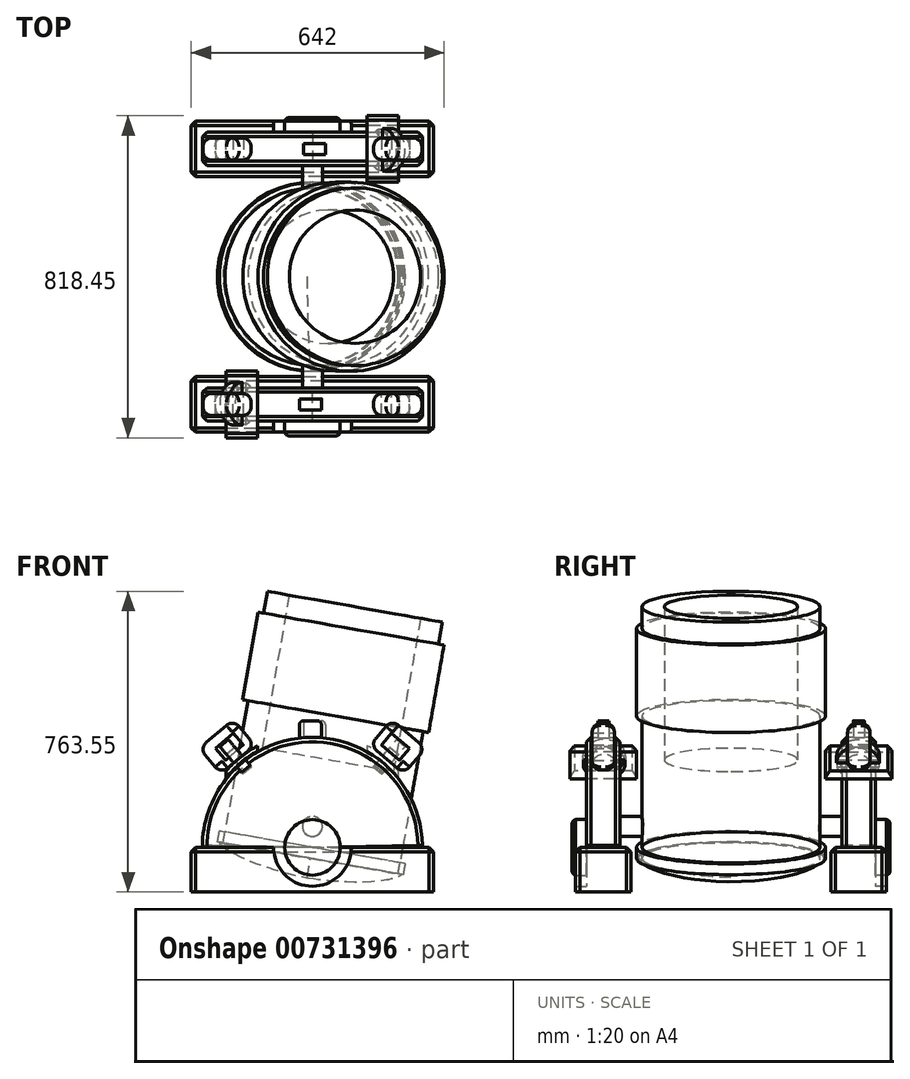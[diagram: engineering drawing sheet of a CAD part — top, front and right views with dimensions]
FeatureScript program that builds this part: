
annotation { "Feature Type Name" : "Feature", "Feature Type Description" : "" }
export const myFeature = defineFeature(function(context is Context, id is Id, definition is map)
    precondition{}
    {
        {
            var Q0;
            Q0=qCreatedBy(makeId("Top.planeOp"),FACE);
            var sketch = newSketch(context, id + "F0", { "sketchPlane" : qUnion([Q0])});
            skCircle(sketch, "E0", {"center": v(0, 0) * mm, "radius": 38.1 * mm});
            skCircle(sketch, "E1", {"center": v(0, 0) * mm, "radius": 50.8 * mm});
            skSolve(sketch);
        }
        {
            var Q0;
            Q0=makeQuery(id+"F0.imprint","IMPRINT",FACE,{"disambiguationData":[TD([[makeQuery(id+"F0.imprint","IMPRINT",EDGE,{"derivedFrom":sQuery(id+"F0.wireOp",EDGE,"E0")}),-1.0]])]});
            extrude(context, id + "F1", {"entities" : qUnion([Q0]), "depth" : 139.7 * mm, "offsetDistance" : 25.4 * mm});
        }
        {
            var Q0;
            Q0=makeQuery(id+"F0.imprint","IMPRINT",FACE,{"disambiguationData":[TD([[makeQuery(id+"F0.imprint","IMPRINT",EDGE,{"derivedFrom":sQuery(id+"F0.wireOp",EDGE,"E0")}),-1.0]])]});
            var Q1;
            Q1=makeQuery(id+"F0.imprint","IMPRINT",FACE,{"disambiguationData":[TD([[makeQuery(id+"F0.imprint","IMPRINT",EDGE,{"derivedFrom":sQuery(id+"F0.wireOp",EDGE,"E0")}),1.0]])]});
            extrude(context, id + "F2", {"entities" : qUnion([Q0, Q1]), "operationType" : NewBodyOperationType.ADD, "depth" : 50.8 * mm, "offsetDistance" : 25.4 * mm});
        }
        {
            var Q0;
            Q0=qCreatedBy(makeId("Top.planeOp"),FACE);
            cPlane(context, id + "F3", {"entities" : qUnion([Q0]), "cplaneType" : CPlaneType.OFFSET, "offset" : 76.2 * mm, "width" : 152.4 * mm, "height" : 152.4 * mm});
        }
        {
            var Q0;
            Q0=qCreatedBy(id+"F3.planeOp",FACE);
            var sketch = newSketch(context, id + "F4", { "sketchPlane" : qUnion([Q0])});
            skCircle(sketch, "E2", {"center": v(0, 0) * mm, "radius": 50.8 * mm});
            skCircle(sketch, "E3", {"center": v(0, 0) * mm, "radius": 53.98 * mm});
            skSolve(sketch);
        }
        {
            var Q0;
            Q0=makeQuery(id+"F4.imprint","IMPRINT",FACE,{"disambiguationData":[TD([[makeQuery(id+"F4.imprint","IMPRINT",EDGE,{"derivedFrom":sQuery(id+"F4.wireOp",EDGE,"E2")}),-1.0]])]});
            extrude(context, id + "F5", {"entities" : qUnion([Q0]), "operationType" : NewBodyOperationType.ADD, "depth" : 50.8 * mm, "offsetDistance" : 25.4 * mm});
        }
        {
            var Q0;
            Q0=qCreatedBy(makeId("Front.planeOp"),FACE);
            cPlane(context, id + "F6", {"entities" : qUnion([Q0]), "cplaneType" : CPlaneType.OFFSET, "offset" : 63.5 * mm, "width" : 152.4 * mm, "height" : 152.4 * mm});
        }
        {
            var Q0;
            Q0=qCreatedBy(id+"F6.planeOp",FACE);
            var sketch = newSketch(context, id + "F7", { "sketchPlane" : qUnion([Q0])});
            skArc(sketch, "E4", {"start": v(45.28, -43.66) * mm, "mid": v(43.66, 45.28) * mm, "end": v(-45.28, 43.66) * mm});
            skLineSegment(sketch, "E5", {"start": v(-45.28, 43.66) * mm, "end": v(45.28, -43.66) * mm});
            skSolve(sketch);
        }
        {
            var Q0;
            Q0=qSketchRegion(id+"F7",true);
            extrude(context, id + "F8", {"entities" : qUnion([Q0]), "depth" : 19.05 * mm});
        }
        {
            var Q0;
            Q0=qCreatedBy(makeId("Top.planeOp"),FACE);
            var sketch = newSketch(context, id + "F9", { "sketchPlane" : qUnion([Q0])});
            skLineSegment(sketch, "E6", {"start": v(0, 0) * mm, "end": v(0, -70.78) * mm});
            skSolve(sketch);
        }
        {
            var Q0;
            Q0=makeQuery(id+"F8.opExtrude","SWEPT_BODY",BODY,{"disambiguationData":[OSD([sQuery(id+"F7.wireOp",EDGE,"E4"),sQuery(id+"F7.wireOp",EDGE,"E5")])]});
            var Q1;
            Q1=sQuery(id+"F9.wireOp",EDGE,"E6");
            transform(context, id + "F10", {"entities" : qUnion([Q0]), "transformType" : TransformType.ROTATION, "transformAxis" : qUnion([Q1]), "angle" : 45 * degree, "makeCopy" : false});
        }
        {
            var Q0;
            Q0=qCreatedBy(makeId("Top.planeOp"),FACE);
            var sketch = newSketch(context, id + "F11", { "sketchPlane" : qUnion([Q0])});
            skLineSegment(sketch, "E7.0.0", {"start": v(-62.9, -63.5) * mm, "end": v(62.9, -63.5) * mm});
            skLineSegment(sketch, "E7.0.1", {"start": v(62.9, -63.5) * mm, "end": v(62.9, -82.55) * mm});
            skLineSegment(sketch, "E7.0.2", {"start": v(62.9, -82.55) * mm, "end": v(-62.9, -82.55) * mm});
            skLineSegment(sketch, "E7.0.3", {"start": v(-62.9, -82.55) * mm, "end": v(-62.9, -63.5) * mm});
            skLineSegment(sketch, "E8", {"start": v(-62.9, -82.55) * mm, "end": v(-69.24, -82.55) * mm});
            skLineSegment(sketch, "E9", {"start": v(-62.9, -82.55) * mm, "end": v(-62.9, -88.9) * mm});
            skLineSegment(sketch, "E10.MirrorCS", {"start": v(62.9, -82.55) * mm, "end": v(62.9, -88.9) * mm});
            skLineSegment(sketch, "E11.MirrorCS", {"start": v(62.9, -82.55) * mm, "end": v(69.24, -82.55) * mm});
            skLineSegment(sketch, "E12", {"start": v(62.9, -63.5) * mm, "end": v(62.9, -57.15) * mm});
            skLineSegment(sketch, "E13", {"start": v(62.9, -63.5) * mm, "end": v(69.24, -63.5) * mm});
            skLineSegment(sketch, "E14.bottom", {"start": v(-69.24, -88.9) * mm, "end": v(69.24, -88.9) * mm});
            skLineSegment(sketch, "E14.top", {"start": v(-69.24, -57.15) * mm, "end": v(69.24, -57.15) * mm});
            skLineSegment(sketch, "E14.left", {"start": v(-69.24, -88.9) * mm, "end": v(-69.24, -57.15) * mm});
            skLineSegment(sketch, "E14.right", {"start": v(69.24, -88.9) * mm, "end": v(69.24, -57.15) * mm});
            skSolve(sketch);
        }
        {
            var Q0;
            {var subQ0=sQuery(id+"F11.wireOp",EDGE,"E12");Q0=makeQuery(id+"F11.imprint","IMPRINT",FACE,{"disambiguationData":[TD([[makeQuery(id+"F11.imprint","IMPRINT",EDGE,{"derivedFrom":subQ0}),-1.0]])]});}
            var Q1;
            Q1=makeQuery(id+"F11.imprint","IMPRINT",FACE,{"disambiguationData":[TD([[makeQuery(id+"F11.imprint","IMPRINT",EDGE,{"derivedFrom":sQuery(id+"F11.wireOp",EDGE,"E7.0.1")}),1.0]])]});
            var Q2;
            Q2=makeQuery(id+"F11.imprint","IMPRINT",FACE,{"disambiguationData":[TD([[makeQuery(id+"F11.imprint","IMPRINT",EDGE,{"derivedFrom":sQuery(id+"F11.wireOp",EDGE,"E7.0.0")}),-1.0]])]});
            var Q3;
            Q3=makeQuery(id+"F11.imprint","IMPRINT",FACE,{"disambiguationData":[TD([[makeQuery(id+"F11.imprint","IMPRINT",EDGE,{"derivedFrom":sQuery(id+"F11.wireOp",EDGE,"E7.0.0")}),1.0]])]});
            var Q4;
            {var subQ0=sQuery(id+"F11.wireOp",EDGE,"E11.MirrorCS");Q4=makeQuery(id+"F11.imprint","IMPRINT",FACE,{"disambiguationData":[TD([[makeQuery(id+"F11.imprint","IMPRINT",EDGE,{"derivedFrom":subQ0}),-1.0]])]});}
            var Q5;
            Q5=makeQuery(id+"F11.imprint","IMPRINT",FACE,{"disambiguationData":[TD([[makeQuery(id+"F11.imprint","IMPRINT",EDGE,{"derivedFrom":sQuery(id+"F11.wireOp",EDGE,"E7.0.2")}),1.0]])]});
            var Q6;
            {var subQ0=sQuery(id+"F11.wireOp",EDGE,"E8");Q6=makeQuery(id+"F11.imprint","IMPRINT",FACE,{"disambiguationData":[TD([[makeQuery(id+"F11.imprint","IMPRINT",EDGE,{"derivedFrom":subQ0}),1.0]])]});}
            extrude(context, id + "F12", {"entities" : qUnion([Q0, Q1, Q2, Q3, Q4, Q5, Q6]), "oppositeDirection" : true, "depth" : 25.4 * mm});
        }
        {
            var Q0;
            Q0=makeQuery(id+"F8.opExtrude","CAP_FACE",FACE,{"disambiguationData":[OSD([sQuery(id+"F7.wireOp",EDGE,"E4"),sQuery(id+"F7.wireOp",EDGE,"E5")])],"isStart":false});
            var sketch = newSketch(context, id + "F13", { "sketchPlane" : qUnion([Q0])});
            skCircle(sketch, "E15", {"center": v(0, 0) * mm, "radius": 22.23 * mm});
            skCircle(sketch, "E16", {"center": v(0, 0) * mm, "radius": 15.88 * mm});
            skSolve(sketch);
        }
        {
            var Q0;
            {var subQ0=sQuery(id+"F13.wireOp",EDGE,"E16");var subQ1=makeQuery(id+"F8.opExtrude","CAP_EDGE",EDGE,{"disambiguationData":[OSD([sQuery(id+"F7.wireOp",EDGE,"E5")])],"isStart":false});var subQ2=makeQuery(id+"F13.imprint","INTERSECT",VERTEX,{"disambiguationData":[OD(0.0)],"derivedFrom":[subQ1,subQ0]});Q0=makeQuery(id+"F13.imprint","IMPRINT",FACE,{"disambiguationData":[TD([[makeQuery(id+"F13.imprint","IMPRINT",EDGE,{"disambiguationData":[TD([[subQ2,-1.0]])],"derivedFrom":subQ0}),1.0]])]});}
            var Q1;
            {var subQ0=sQuery(id+"F13.wireOp",EDGE,"E16");var subQ1=makeQuery(id+"F8.opExtrude","CAP_EDGE",EDGE,{"disambiguationData":[OSD([sQuery(id+"F7.wireOp",EDGE,"E5")])],"isStart":false});var subQ2=makeQuery(id+"F13.imprint","INTERSECT",VERTEX,{"disambiguationData":[OD(0.0)],"derivedFrom":[subQ1,subQ0]});Q1=makeQuery(id+"F13.imprint","IMPRINT",FACE,{"disambiguationData":[TD([[makeQuery(id+"F13.imprint","IMPRINT",EDGE,{"disambiguationData":[TD([[subQ2,1.0]])],"derivedFrom":subQ0}),1.0]])]});}
            extrude(context, id + "F14", {"entities" : qUnion([Q0, Q1]), "operationType" : NewBodyOperationType.ADD, "depth" : 8.38 * mm, "offsetDistance" : 25.4 * mm});
        }
        {
            var Q0;
            {var subQ0=sQuery(id+"F13.wireOp",EDGE,"E15");var subQ1=makeQuery(id+"F8.opExtrude","CAP_EDGE",EDGE,{"disambiguationData":[OSD([sQuery(id+"F7.wireOp",EDGE,"E5")])],"isStart":false});var subQ2=makeQuery(id+"F13.imprint","INTERSECT",VERTEX,{"disambiguationData":[OD(0.0)],"derivedFrom":[subQ1,subQ0]});Q0=makeQuery(id+"F13.imprint","IMPRINT",FACE,{"disambiguationData":[TD([[makeQuery(id+"F13.imprint","IMPRINT",EDGE,{"disambiguationData":[TD([[subQ2,-1.0]])],"derivedFrom":subQ0}),1.0]])]});}
            var Q1;
            {var subQ0=sQuery(id+"F13.wireOp",EDGE,"E15");var subQ1=makeQuery(id+"F8.opExtrude","CAP_EDGE",EDGE,{"disambiguationData":[OSD([sQuery(id+"F7.wireOp",EDGE,"E5")])],"isStart":false});var subQ2=makeQuery(id+"F13.imprint","INTERSECT",VERTEX,{"disambiguationData":[OD(0.0)],"derivedFrom":[subQ1,subQ0]});Q1=makeQuery(id+"F13.imprint","IMPRINT",FACE,{"disambiguationData":[TD([[makeQuery(id+"F13.imprint","IMPRINT",EDGE,{"disambiguationData":[TD([[subQ2,1.0]])],"derivedFrom":subQ0}),1.0]])]});}
            extrude(context, id + "F15", {"entities" : qUnion([Q0, Q1]), "operationType" : NewBodyOperationType.ADD, "depth" : 6.35 * mm, "offsetDistance" : 25.4 * mm});
        }
        {
            var Q0;
            Q0=makeQuery(id+"F15.opExtrude","CAP_EDGE",EDGE,{"disambiguationData":[OSD([sQuery(id+"F13.wireOp",EDGE,"E15")])],"isStart":false});
            var Q1;
            Q1=makeQuery(id+"F14.opExtrude","CAP_EDGE",EDGE,{"disambiguationData":[OSD([sQuery(id+"F13.wireOp",EDGE,"E16")])],"isStart":false});
            fillet(context, id + "F16", {"entities" : qUnion([Q0, Q1]), "radius" : 2.54 * mm, "tangentPropagation" : true, "allowEdgeOverflow" : false});
        }
        {
            var Q0;
            Q0=qSketchRegion(id+"F13",true);
            var Q1;
            Q1=sQuery(id+"F13.wireOp",EDGE,"E15");
            extrude(context, id + "F17", {"entities" : qUnion([Q0]), "operationType" : NewBodyOperationType.REMOVE, "surfaceEntities" : qUnion([Q1]), "depth" : 25.4 * mm});
        }
        {
            var Q0;
            Q0=makeQuery(id+"F8.opExtrude","SWEPT_BODY",BODY,{"disambiguationData":[OSD([sQuery(id+"F7.wireOp",EDGE,"E4"),sQuery(id+"F7.wireOp",EDGE,"E5")])]});
            var Q1;
            Q1=makeQuery(id+"F14.opExtrude","SWEPT_BODY",BODY,{"disambiguationData":[OSD([sQuery(id+"F13.wireOp",EDGE,"E16")])]});
            var Q2;
            Q2=makeQuery(id+"F15.opExtrude","SWEPT_BODY",BODY,{"disambiguationData":[OSD([sQuery(id+"F13.wireOp",EDGE,"E15"),sQuery(id+"F13.wireOp",EDGE,"E16")])]});
            var Q3;
            Q3=makeQuery(id+"F17.boolean.opBoolean","SPLIT",BODY,{"disambiguationData":[OD(0.0)],"derivedFrom":makeQuery(id+"F12.opExtrude","SWEPT_BODY",BODY,{"disambiguationData":[OSD([sQuery(id+"F11.wireOp",EDGE,"E7.0.0"),sQuery(id+"F11.wireOp",EDGE,"E7.0.1"),sQuery(id+"F11.wireOp",EDGE,"E7.0.2"),sQuery(id+"F11.wireOp",EDGE,"E7.0.3"),sQuery(id+"F11.wireOp",EDGE,"E14.bottom"),sQuery(id+"F11.wireOp",EDGE,"E14.top"),sQuery(id+"F11.wireOp",EDGE,"E14.left"),sQuery(id+"F11.wireOp",EDGE,"E14.right")])]})});
            var Q4;
            Q4=makeQuery(id+"F17.boolean.opBoolean","SPLIT",BODY,{"disambiguationData":[OD(1.0)],"derivedFrom":makeQuery(id+"F12.opExtrude","SWEPT_BODY",BODY,{"disambiguationData":[OSD([sQuery(id+"F11.wireOp",EDGE,"E7.0.0"),sQuery(id+"F11.wireOp",EDGE,"E7.0.1"),sQuery(id+"F11.wireOp",EDGE,"E7.0.2"),sQuery(id+"F11.wireOp",EDGE,"E7.0.3"),sQuery(id+"F11.wireOp",EDGE,"E14.bottom"),sQuery(id+"F11.wireOp",EDGE,"E14.top"),sQuery(id+"F11.wireOp",EDGE,"E14.left"),sQuery(id+"F11.wireOp",EDGE,"E14.right")])]})});
            var Q5;
            Q5=makeQuery(id+"F1.opExtrude","SWEPT_FACE",FACE,{"disambiguationData":[OSD([sQuery(id+"F0.wireOp",EDGE,"E0")])]});
            transform(context, id + "F18", {"entities" : qUnion([Q0, Q1, Q2, Q3, Q4]), "transformType" : TransformType.ROTATION, "transformAxis" : qUnion([Q5]), "angle" : 180 * degree, "makeCopy" : true});
        }
        {
            var Q0;
            Q0=makeQuery(id+"F18.opPattern","COPY",BODY,{"derivedFrom":makeQuery(id+"F8.opExtrude","SWEPT_BODY",BODY,{"disambiguationData":[OSD([sQuery(id+"F7.wireOp",EDGE,"E4"),sQuery(id+"F7.wireOp",EDGE,"E5")])]}),"instanceName":"1"});
            var Q1;
            Q1=makeQuery(id+"F18.opPattern","COPY",BODY,{"derivedFrom":makeQuery(id+"F14.opExtrude","SWEPT_BODY",BODY,{"disambiguationData":[OSD([sQuery(id+"F13.wireOp",EDGE,"E16")])]}),"instanceName":"1"});
            var Q2;
            Q2=makeQuery(id+"F18.opPattern","COPY",BODY,{"derivedFrom":makeQuery(id+"F15.opExtrude","SWEPT_BODY",BODY,{"disambiguationData":[OSD([sQuery(id+"F13.wireOp",EDGE,"E15"),sQuery(id+"F13.wireOp",EDGE,"E16")])]}),"instanceName":"1"});
            var Q3;
            Q3=makeQuery(id+"F18.opPattern","COPY",BODY,{"derivedFrom":makeQuery(id+"F17.boolean.opBoolean","SPLIT",BODY,{"disambiguationData":[OD(0.0)],"derivedFrom":makeQuery(id+"F12.opExtrude","SWEPT_BODY",BODY,{"disambiguationData":[OSD([sQuery(id+"F11.wireOp",EDGE,"E7.0.0"),sQuery(id+"F11.wireOp",EDGE,"E7.0.1"),sQuery(id+"F11.wireOp",EDGE,"E7.0.2"),sQuery(id+"F11.wireOp",EDGE,"E7.0.3"),sQuery(id+"F11.wireOp",EDGE,"E14.bottom"),sQuery(id+"F11.wireOp",EDGE,"E14.top"),sQuery(id+"F11.wireOp",EDGE,"E14.left"),sQuery(id+"F11.wireOp",EDGE,"E14.right")])]})}),"instanceName":"1"});
            var Q4;
            Q4=makeQuery(id+"F18.opPattern","COPY",BODY,{"derivedFrom":makeQuery(id+"F17.boolean.opBoolean","SPLIT",BODY,{"disambiguationData":[OD(1.0)],"derivedFrom":makeQuery(id+"F12.opExtrude","SWEPT_BODY",BODY,{"disambiguationData":[OSD([sQuery(id+"F11.wireOp",EDGE,"E7.0.0"),sQuery(id+"F11.wireOp",EDGE,"E7.0.1"),sQuery(id+"F11.wireOp",EDGE,"E7.0.2"),sQuery(id+"F11.wireOp",EDGE,"E7.0.3"),sQuery(id+"F11.wireOp",EDGE,"E14.bottom"),sQuery(id+"F11.wireOp",EDGE,"E14.top"),sQuery(id+"F11.wireOp",EDGE,"E14.left"),sQuery(id+"F11.wireOp",EDGE,"E14.right")])]})}),"instanceName":"1"});
            deleteBodies(context, id + "F19", {"entities" : qUnion([Q0, Q1, Q2, Q3, Q4])});
        }
        {
            var Q0;
            {var subQ1=sQuery(id+"F11.wireOp",EDGE,"E14.left");var subQ3=sQuery(id+"F11.wireOp",EDGE,"E14.bottom");Q0=makeQuery(id+"F17.boolean.opBoolean","SPLIT",FACE,{"disambiguationData":[TD([makeQuery(id+"F12.opExtrude","SWEPT_FACE",FACE,{"disambiguationData":[OSD([subQ1])]})])],"derivedFrom":makeQuery(id+"F12.opExtrude","SWEPT_FACE",FACE,{"disambiguationData":[OSD([subQ3])]})});}
            cPlane(context, id + "F20", {"entities" : qUnion([Q0]), "cplaneType" : CPlaneType.OFFSET, "offset" : 3.17 * mm, "width" : 152.4 * mm, "height" : 152.4 * mm});
        }
        {
            var Q0;
            Q0=qCreatedBy(id+"F20.planeOp",FACE);
            var sketch = newSketch(context, id + "F21", { "sketchPlane" : qUnion([Q0])});
            skArc(sketch, "E17.0", {"start": v(62.9, 1.15) * mm, "mid": v(-1.15, 62.9) * mm, "end": v(-62.9, -1.15) * mm});
            skLineSegment(sketch, "E18.0", {"start": v(-69.24, -25.4) * mm, "end": v(69.24, -25.4) * mm});
            skLineSegment(sketch, "E19", {"start": v(-49.3, -25.4) * mm, "end": v(-49.3, 43.8) * mm});
            skLineSegment(sketch, "E20", {"start": v(-49.3, -25.4) * mm, "end": v(-31.25, -25.4) * mm});
            skLineSegment(sketch, "E21", {"start": v(-31.25, -25.4) * mm, "end": v(-31.25, 58.08) * mm});
            skArc(sketch, "E22", {"start": v(-31.25, 58.08) * mm, "mid": v(-40.9, 51.74) * mm, "end": v(-49.3, 43.8) * mm});
            skArc(sketch, "E23.trimOffspring", {"start": v(-60.86, -25.4) * mm, "mid": v(0, -65.95) * mm, "end": v(60.86, -25.4) * mm});
            skSolve(sketch);
        }
        {
            var Q0;
            {var subQ5=sQuery(id+"F21.wireOp",EDGE,"E20");Q0=makeQuery(id+"F21.imprint","IMPRINT",FACE,{"disambiguationData":[TD([[makeQuery(id+"F21.imprint","IMPRINT",EDGE,{"derivedFrom":subQ5}),1.0]])]});}
            var Q1;
            {var subQ5=sQuery(id+"F21.wireOp",EDGE,"E22");Q1=makeQuery(id+"F21.imprint","IMPRINT",FACE,{"disambiguationData":[TD([[makeQuery(id+"F21.imprint","IMPRINT",EDGE,{"derivedFrom":subQ5}),1.0]])]});}
            extrude(context, id + "F22", {"entities" : qUnion([Q0, Q1]), "oppositeDirection" : true, "depth" : 38.1 * mm});
        }
        {
            var Q0;
            Q0=makeQuery(id+"F8.opExtrude","CAP_FACE",FACE,{"disambiguationData":[OSD([sQuery(id+"F7.wireOp",EDGE,"E4"),sQuery(id+"F7.wireOp",EDGE,"E5")])],"isStart":false});
            cPlane(context, id + "F23", {"entities" : qUnion([Q0]), "cplaneType" : CPlaneType.OFFSET, "offset" : 9.52 * mm, "oppositeDirection" : true, "width" : 152.4 * mm, "height" : 152.4 * mm});
        }
        {
            var Q0;
            Q0=qCreatedBy(id+"F23.planeOp",FACE);
            var sketch = newSketch(context, id + "F24", { "sketchPlane" : qUnion([Q0])});
            skPoint(sketch, "E24.0", {"position": v(-1.15, 62.9) * mm});
            skLineSegment(sketch, "E25.bottom", {"start": v(5.2, 72.42) * mm, "end": v(-7.5, 72.42) * mm});
            skLineSegment(sketch, "E25.top", {"start": v(5.2, 53.37) * mm, "end": v(-7.5, 53.37) * mm});
            skLineSegment(sketch, "E25.left", {"start": v(5.2, 72.42) * mm, "end": v(5.2, 53.37) * mm});
            skLineSegment(sketch, "E25.right", {"start": v(-7.5, 72.42) * mm, "end": v(-7.5, 53.37) * mm});
            skSolve(sketch);
        }
        {
            var Q0;
            Q0=makeQuery(id+"F24.imprint","IMPRINT",FACE,{"disambiguationData":[TD([[makeQuery(id+"F24.imprint","IMPRINT",EDGE,{"derivedFrom":sQuery(id+"F24.wireOp",EDGE,"E25.bottom")}),1.0]])]});
            extrude(context, id + "F25", {"entities" : qUnion([Q0]), "operationType" : NewBodyOperationType.ADD, "endBound" : BoundingType.SYMMETRIC, "depth" : 6.35 * mm, "offsetDistance" : 25.4 * mm});
        }
        {
            var Q0;
            Q0=makeQuery(id+"F25.opExtrude","SWEPT_EDGE",EDGE,{"disambiguationData":[OSD([sQuery(id+"F24.wireOp",EDGE,"E25.bottom"),sQuery(id+"F24.wireOp",EDGE,"E25.right")])]});
            var Q1;
            Q1=makeQuery(id+"F25.opExtrude","SWEPT_EDGE",EDGE,{"disambiguationData":[OSD([sQuery(id+"F24.wireOp",EDGE,"E25.bottom"),sQuery(id+"F24.wireOp",EDGE,"E25.left")])]});
            fillet(context, id + "F26", {"entities" : qUnion([Q0, Q1]), "radius" : 2.54 * mm, "tangentPropagation" : true, "allowEdgeOverflow" : false});
        }
        {
            var Q0;
            Q0=makeQuery(id+"F22.opExtrude","CAP_EDGE",EDGE,{"disambiguationData":[OSD([sQuery(id+"F21.wireOp",EDGE,"E22")])],"isStart":true});
            var Q1;
            Q1=makeQuery(id+"FDD8fb37NUxeniG_7.opPattern","COPY",EDGE,{"derivedFrom":makeQuery(id+"F22.opExtrude","CAP_EDGE",EDGE,{"disambiguationData":[OSD([sQuery(id+"F21.wireOp",EDGE,"E22")])],"isStart":true}),"instanceName":"1"});
            var Q2;
            {var subQ0=sQuery(id+"F11.wireOp",EDGE,"E14.left");var subQ1=sQuery(id+"F11.wireOp",EDGE,"E14.bottom");Q2=makeQuery(id+"F17.boolean.opBoolean","SPLIT",EDGE,{"disambiguationData":[TD([makeQuery(id+"F12.opExtrude","SWEPT_FACE",FACE,{"disambiguationData":[OSD([subQ0])]})])],"derivedFrom":makeQuery(id+"F12.opExtrude","CAP_EDGE",EDGE,{"disambiguationData":[OSD([subQ1])],"isStart":true})});}
            var Q3;
            {var subQ0=sQuery(id+"F11.wireOp",EDGE,"E14.right");var subQ1=sQuery(id+"F11.wireOp",EDGE,"E14.bottom");Q3=makeQuery(id+"F17.boolean.opBoolean","SPLIT",EDGE,{"disambiguationData":[TD([makeQuery(id+"F12.opExtrude","SWEPT_FACE",FACE,{"disambiguationData":[OSD([subQ0])]})])],"derivedFrom":makeQuery(id+"F12.opExtrude","CAP_EDGE",EDGE,{"disambiguationData":[OSD([subQ1])],"isStart":true})});}
            var Q4;
            Q4=makeQuery(id+"F12.opExtrude","CAP_EDGE",EDGE,{"disambiguationData":[OSD([sQuery(id+"F11.wireOp",EDGE,"E14.left")])],"isStart":true});
            var Q5;
            Q5=makeQuery(id+"F12.opExtrude","SWEPT_EDGE",EDGE,{"disambiguationData":[OSD([sQuery(id+"F11.wireOp",EDGE,"E14.bottom"),sQuery(id+"F11.wireOp",EDGE,"E14.left")])]});
            var Q6;
            Q6=makeQuery(id+"F22.opExtrude","CAP_EDGE",EDGE,{"disambiguationData":[OSD([sQuery(id+"F21.wireOp",EDGE,"E22")])],"isStart":false});
            var Q7;
            Q7=makeQuery(id+"F8.opExtrude","CAP_EDGE",EDGE,{"disambiguationData":[OSD([sQuery(id+"F7.wireOp",EDGE,"E4")])],"isStart":false});
            var Q8;
            Q8=makeQuery(id+"F8.opExtrude","CAP_EDGE",EDGE,{"disambiguationData":[OSD([sQuery(id+"F7.wireOp",EDGE,"E4")])],"isStart":true});
            var Q9;
            Q9=makeQuery(id+"F12.opExtrude","CAP_EDGE",EDGE,{"disambiguationData":[OSD([sQuery(id+"F11.wireOp",EDGE,"E14.top")])],"isStart":true});
            var Q10;
            Q10=makeQuery(id+"F12.opExtrude","SWEPT_EDGE",EDGE,{"disambiguationData":[OSD([sQuery(id+"F11.wireOp",EDGE,"E14.top"),sQuery(id+"F11.wireOp",EDGE,"E14.left")])]});
            var Q11;
            Q11=makeQuery(id+"F12.opExtrude","SWEPT_EDGE",EDGE,{"disambiguationData":[OSD([sQuery(id+"F11.wireOp",EDGE,"E14.bottom"),sQuery(id+"F11.wireOp",EDGE,"E14.right")])]});
            var Q12;
            Q12=makeQuery(id+"F12.opExtrude","CAP_EDGE",EDGE,{"disambiguationData":[OSD([sQuery(id+"F11.wireOp",EDGE,"E14.right")])],"isStart":true});
            var Q13;
            Q13=makeQuery(id+"FDD8fb37NUxeniG_7.opPattern","COPY",EDGE,{"derivedFrom":makeQuery(id+"F22.opExtrude","CAP_EDGE",EDGE,{"disambiguationData":[OSD([sQuery(id+"F21.wireOp",EDGE,"E22")])],"isStart":false}),"instanceName":"1"});
            var Q14;
            Q14=makeQuery(id+"F12.opExtrude","SWEPT_EDGE",EDGE,{"disambiguationData":[OSD([sQuery(id+"F11.wireOp",EDGE,"E14.top"),sQuery(id+"F11.wireOp",EDGE,"E14.right")])]});
            chamfer(context, id + "F27", {"entities" : qUnion([Q0, Q1, Q2, Q3, Q4, Q5, Q6, Q7, Q8, Q9, Q10, Q11, Q12, Q13, Q14]), "width" : 2.54 * mm, "tangentPropagation" : true});
        }
        {
            var Q0;
            {var subQ0=sQuery(id+"F21.wireOp",EDGE,"E22");Q0=makeQuery(id+"F27.opChamfer","BLEND_EDGE",EDGE,{"blendedFrom":[makeQuery(id+"F22.opExtrude","CAP_EDGE",EDGE,{"disambiguationData":[OSD([subQ0])],"isStart":true}),makeQuery(id+"F22.opExtrude","CAP_FACE",FACE,{"disambiguationData":[OSD([sQuery(id+"F21.wireOp",EDGE,"E19"),sQuery(id+"F21.wireOp",EDGE,"E21"),subQ0,sQuery(id+"F21.wireOp",EDGE,"E20")])],"isStart":true})],"blendedInto":[makeQuery(id+"F22.opExtrude","CAP_FACE",FACE,{"disambiguationData":[OSD([sQuery(id+"F21.wireOp",EDGE,"E19"),sQuery(id+"F21.wireOp",EDGE,"E21"),subQ0,sQuery(id+"F21.wireOp",EDGE,"E20")])],"isStart":true})]});}
            cPoint(context, id + "F28", {"entities" : qUnion([Q0]), "parameter" : 0.5});
        }
        {
            var Q0;
            {var subQ0=sQuery(id+"F7.wireOp",EDGE,"E4");Q0=makeQuery(id+"F27.opChamfer","BLEND_EDGE",EDGE,{"blendedFrom":[makeQuery(id+"F8.opExtrude","CAP_EDGE",EDGE,{"disambiguationData":[OSD([subQ0])],"isStart":false}),makeQuery(id+"F8.opExtrude","SWEPT_FACE",FACE,{"disambiguationData":[OSD([subQ0])]})],"blendedInto":[makeQuery(id+"F8.opExtrude","SWEPT_FACE",FACE,{"disambiguationData":[OSD([subQ0])]})]});}
            var Q1;
            Q1=qCreatedBy(id+"F28",VERTEX);
            cPlane(context, id + "F29", {"entities" : qUnion([Q0, Q1]), "cplaneType" : CPlaneType.CURVE_POINT, "offset" : 25.4 * mm, "width" : 152.4 * mm, "height" : 152.4 * mm});
        }
        {
            var Q0;
            Q0=qCreatedBy(id+"F29.planeOp",FACE);
            var sketch = newSketch(context, id + "F30", { "sketchPlane" : qUnion([Q0])});
            skLineSegment(sketch, "E26", {"start": v(-76.83, 65.95) * mm, "end": v(-68.32, 65.95) * mm});
            skCircle(sketch, "E27", {"center": v(-72.58, 65.95) * mm, "radius": 12.21 * mm});
            skCircle(sketch, "E28", {"center": v(-72.58, 65.95) * mm, "radius": 6.35 * mm});
            skSolve(sketch);
        }
        {
            var Q0;
            {var subQ0=sQuery(id+"F30.wireOp",EDGE,"E27");var subQ1=sQuery(id+"F30.wireOp",EDGE,"E26");var subQ2=makeQuery(id+"F30.imprint","INTERSECT",VERTEX,{"disambiguationData":[OD(0.0)],"derivedFrom":[subQ1,subQ0]});Q0=makeQuery(id+"F30.imprint","IMPRINT",FACE,{"disambiguationData":[TD([[makeQuery(id+"F30.imprint","IMPRINT",EDGE,{"disambiguationData":[TD([[subQ2,-1.0]])],"derivedFrom":subQ1}),1.0]])]});}
            var Q1;
            Q1=makeQuery(id+"F30.imprint","IMPRINT",FACE,{"disambiguationData":[TD([[makeQuery(id+"F30.imprint","IMPRINT",EDGE,{"derivedFrom":sQuery(id+"F30.wireOp",EDGE,"E27")}),1.0]])]});
            extrude(context, id + "F31", {"entities" : qUnion([Q0, Q1]), "operationType" : NewBodyOperationType.ADD, "endBound" : BoundingType.SYMMETRIC, "depth" : 6.35 * mm, "offsetDistance" : 25.4 * mm});
        }
        {
            var Q0;
            Q0=qCreatedBy(id+"F29.planeOp",FACE);
            var sketch = newSketch(context, id + "F32", { "sketchPlane" : qUnion([Q0])});
            skLineSegment(sketch, "E29.0", {"start": v(-66.23, 65.95) * mm, "end": v(-66.23, 65.95) * mm});
            skCircle(sketch, "E30", {"center": v(-72.58, 65.95) * mm, "radius": 6.35 * mm});
            skSolve(sketch);
        }
        {
            var Q0;
            Q0=qCreatedBy(id+"F23.planeOp",FACE);
            var sketch = newSketch(context, id + "F33", { "sketchPlane" : qUnion([Q0])});
            skLineSegment(sketch, "E31.0", {"start": v(-46.74, 55.16) * mm, "end": v(-38.53, 45.47) * mm});
            skLineSegment(sketch, "E32", {"start": v(-42.63, 50.32) * mm, "end": v(-52.32, 42.1) * mm});
            skLineSegment(sketch, "E33", {"start": v(-41.15, 68.22) * mm, "end": v(-41.15, 68.22) * mm});
            skPoint(sketch, "E34.startSnap0", {"position": v(-41.15, 68.22) * mm});
            skLineSegment(sketch, "E35", {"start": v(-42.63, 50.32) * mm, "end": v(-32.94, 58.53) * mm});
            skLineSegment(sketch, "E36", {"start": v(-32.94, 58.53) * mm, "end": v(-45.26, 73.06) * mm});
            skLineSegment(sketch, "E37", {"start": v(-45.26, 73.06) * mm, "end": v(-64.64, 56.64) * mm});
            skLineSegment(sketch, "E38", {"start": v(-64.64, 56.64) * mm, "end": v(-52.32, 42.1) * mm});
            skLineSegment(sketch, "E39", {"start": v(-42.63, 50.32) * mm, "end": v(-44.18, 52.14) * mm});
            skLineSegment(sketch, "E40", {"start": v(-55.52, 56.64) * mm, "end": v(-45.26, 65.34) * mm});
            skLineSegment(sketch, "E41", {"start": v(-45.26, 65.34) * mm, "end": v(-39.49, 58.53) * mm});
            skLineSegment(sketch, "E42", {"start": v(-39.49, 58.53) * mm, "end": v(-49.75, 49.83) * mm});
            skPoint(sketch, "E42.endSnap0", {"position": v(-47.48, 46.21) * mm});
            skLineSegment(sketch, "E43", {"start": v(-49.75, 49.83) * mm, "end": v(-55.52, 56.64) * mm});
            skSolve(sketch);
        }
        {
            var Q0;
            Q0=makeQuery(id+"F33.imprint","IMPRINT",FACE,{"disambiguationData":[TD([[makeQuery(id+"F33.imprint","IMPRINT",EDGE,{"derivedFrom":sQuery(id+"F33.wireOp",EDGE,"E32")}),-1.0]])]});
            extrude(context, id + "F34", {"entities" : qUnion([Q0]), "endBound" : BoundingType.SYMMETRIC, "depth" : 12.7 * mm, "offsetDistance" : 25.4 * mm});
        }
        {
            var Q0;
            Q0=makeQuery(id+"F34.opExtrude","SWEPT_EDGE",EDGE,{"disambiguationData":[OSD([sQuery(id+"F33.wireOp",EDGE,"E37"),sQuery(id+"F33.wireOp",EDGE,"E38")])]});
            var Q1;
            Q1=makeQuery(id+"F34.opExtrude","SWEPT_EDGE",EDGE,{"disambiguationData":[OSD([sQuery(id+"F33.wireOp",EDGE,"E36"),sQuery(id+"F33.wireOp",EDGE,"E37")])]});
            var Q2;
            Q2=makeQuery(id+"F34.opExtrude","SWEPT_EDGE",EDGE,{"disambiguationData":[OSD([sQuery(id+"F33.wireOp",EDGE,"E32"),sQuery(id+"F33.wireOp",EDGE,"E38")])]});
            var Q3;
            Q3=makeQuery(id+"F34.opExtrude","SWEPT_EDGE",EDGE,{"disambiguationData":[OSD([sQuery(id+"F33.wireOp",EDGE,"E35"),sQuery(id+"F33.wireOp",EDGE,"E36")])]});
            var Q4;
            Q4=makeQuery(id+"F34.opExtrude","CAP_EDGE",EDGE,{"disambiguationData":[OSD([sQuery(id+"F33.wireOp",EDGE,"E37")])],"isStart":false});
            var Q5;
            Q5=makeQuery(id+"F34.opExtrude","CAP_EDGE",EDGE,{"disambiguationData":[OSD([sQuery(id+"F33.wireOp",EDGE,"E37")])],"isStart":true});
            var Q6;
            Q6=makeQuery(id+"F34.opExtrude","CAP_EDGE",EDGE,{"disambiguationData":[OSD([sQuery(id+"F33.wireOp",EDGE,"E38")])],"isStart":false});
            var Q7;
            Q7=makeQuery(id+"F34.opExtrude","CAP_EDGE",EDGE,{"disambiguationData":[OSD([sQuery(id+"F33.wireOp",EDGE,"E38")])],"isStart":true});
            fillet(context, id + "F35", {"entities" : qUnion([Q0, Q1, Q2, Q3, Q4, Q5, Q6, Q7]), "radius" : 5.08 * mm, "tangentPropagation" : true, "allowEdgeOverflow" : false});
        }
        {
            var Q0;
            {var subQ0=sQuery(id+"F33.wireOp",EDGE,"E36");var subQ1=sQuery(id+"F33.wireOp",EDGE,"E35");Q0=makeQuery(id+"F35.opFillet","BLEND_EDGE",EDGE,{"blendedFrom":[makeQuery(id+"F34.opExtrude","SWEPT_EDGE",EDGE,{"disambiguationData":[OSD([subQ1,subQ0])]}),makeQuery(id+"F34.opExtrude","CAP_FACE",FACE,{"disambiguationData":[OSD([sQuery(id+"F33.wireOp",EDGE,"E32"),subQ1,subQ0,sQuery(id+"F33.wireOp",EDGE,"E37"),sQuery(id+"F33.wireOp",EDGE,"E38"),sQuery(id+"F33.wireOp",EDGE,"E40"),sQuery(id+"F33.wireOp",EDGE,"E41"),sQuery(id+"F33.wireOp",EDGE,"E42"),sQuery(id+"F33.wireOp",EDGE,"E43")])],"isStart":false})],"blendedInto":[makeQuery(id+"F34.opExtrude","CAP_FACE",FACE,{"disambiguationData":[OSD([sQuery(id+"F33.wireOp",EDGE,"E32"),subQ1,subQ0,sQuery(id+"F33.wireOp",EDGE,"E37"),sQuery(id+"F33.wireOp",EDGE,"E38"),sQuery(id+"F33.wireOp",EDGE,"E40"),sQuery(id+"F33.wireOp",EDGE,"E41"),sQuery(id+"F33.wireOp",EDGE,"E42"),sQuery(id+"F33.wireOp",EDGE,"E43")])],"isStart":false})]});}
            var Q1;
            {var subQ0=sQuery(id+"F33.wireOp",EDGE,"E37");Q1=makeQuery(id+"F35.opFillet","BLEND_EDGE",EDGE,{"blendedFrom":[makeQuery(id+"F34.opExtrude","SWEPT_EDGE",EDGE,{"disambiguationData":[OSD([sQuery(id+"F33.wireOp",EDGE,"E36"),subQ0])]}),makeQuery(id+"F34.opExtrude","CAP_EDGE",EDGE,{"disambiguationData":[OSD([subQ0])],"isStart":true})],"blendedInto":[]});}
            fillet(context, id + "F36", {"entities" : qUnion([Q0, Q1]), "radius" : 5.08 * mm, "tangentPropagation" : true, "allowEdgeOverflow" : false});
        }
        {
            var Q0;
            Q0=makeQuery(id+"F22.opExtrude","SWEPT_BODY",BODY,{"disambiguationData":[OSD([sQuery(id+"F21.wireOp",EDGE,"E19"),sQuery(id+"F21.wireOp",EDGE,"E21"),sQuery(id+"F21.wireOp",EDGE,"E22"),sQuery(id+"F21.wireOp",EDGE,"E20")])]});
            var Q1;
            Q1=makeQuery(id+"F31.opExtrude","SWEPT_BODY",BODY,{"disambiguationData":[OSD([sQuery(id+"F30.wireOp",EDGE,"E26"),sQuery(id+"F30.wireOp",EDGE,"E27"),sQuery(id+"F30.wireOp",EDGE,"E28")])]});
            var Q2;
            Q2=makeQuery(id+"F34.opExtrude","SWEPT_BODY",BODY,{"disambiguationData":[OSD([sQuery(id+"F33.wireOp",EDGE,"E32"),sQuery(id+"F33.wireOp",EDGE,"E35"),sQuery(id+"F33.wireOp",EDGE,"E36"),sQuery(id+"F33.wireOp",EDGE,"E37"),sQuery(id+"F33.wireOp",EDGE,"E38"),sQuery(id+"F33.wireOp",EDGE,"E40"),sQuery(id+"F33.wireOp",EDGE,"E41"),sQuery(id+"F33.wireOp",EDGE,"E42"),sQuery(id+"F33.wireOp",EDGE,"E43")])]});
            var Q3;
            Q3=qCreatedBy(makeId("Right.planeOp"),FACE);
            mirror(context, id + "F37", {"entities" : qUnion([Q0, Q1, Q2]), "mirrorPlane" : qUnion([Q3])});
        }
        {
            var Q0;
            Q0=makeQuery(id+"F8.opExtrude","SWEPT_BODY",BODY,{"disambiguationData":[OSD([sQuery(id+"F7.wireOp",EDGE,"E4"),sQuery(id+"F7.wireOp",EDGE,"E5")])]});
            var Q1;
            Q1=makeQuery(id+"F14.opExtrude","SWEPT_BODY",BODY,{"disambiguationData":[OSD([sQuery(id+"F13.wireOp",EDGE,"E16")])]});
            var Q2;
            Q2=makeQuery(id+"F15.opExtrude","SWEPT_BODY",BODY,{"disambiguationData":[OSD([sQuery(id+"F13.wireOp",EDGE,"E15"),sQuery(id+"F13.wireOp",EDGE,"E16")])]});
            var Q3;
            Q3=makeQuery(id+"F17.boolean.opBoolean","SPLIT",BODY,{"disambiguationData":[OD(0.0)],"derivedFrom":makeQuery(id+"F12.opExtrude","SWEPT_BODY",BODY,{"disambiguationData":[OSD([sQuery(id+"F11.wireOp",EDGE,"E7.0.0"),sQuery(id+"F11.wireOp",EDGE,"E7.0.1"),sQuery(id+"F11.wireOp",EDGE,"E7.0.2"),sQuery(id+"F11.wireOp",EDGE,"E7.0.3"),sQuery(id+"F11.wireOp",EDGE,"E14.bottom"),sQuery(id+"F11.wireOp",EDGE,"E14.top"),sQuery(id+"F11.wireOp",EDGE,"E14.left"),sQuery(id+"F11.wireOp",EDGE,"E14.right")])]})});
            var Q4;
            Q4=makeQuery(id+"F17.boolean.opBoolean","SPLIT",BODY,{"disambiguationData":[OD(1.0)],"derivedFrom":makeQuery(id+"F12.opExtrude","SWEPT_BODY",BODY,{"disambiguationData":[OSD([sQuery(id+"F11.wireOp",EDGE,"E7.0.0"),sQuery(id+"F11.wireOp",EDGE,"E7.0.1"),sQuery(id+"F11.wireOp",EDGE,"E7.0.2"),sQuery(id+"F11.wireOp",EDGE,"E7.0.3"),sQuery(id+"F11.wireOp",EDGE,"E14.bottom"),sQuery(id+"F11.wireOp",EDGE,"E14.top"),sQuery(id+"F11.wireOp",EDGE,"E14.left"),sQuery(id+"F11.wireOp",EDGE,"E14.right")])]})});
            var Q5;
            Q5=makeQuery(id+"F22.opExtrude","SWEPT_BODY",BODY,{"disambiguationData":[OSD([sQuery(id+"F21.wireOp",EDGE,"E19"),sQuery(id+"F21.wireOp",EDGE,"E21"),sQuery(id+"F21.wireOp",EDGE,"E22"),sQuery(id+"F21.wireOp",EDGE,"E20")])]});
            var Q6;
            Q6=makeQuery(id+"F25.opExtrude","SWEPT_BODY",BODY,{"disambiguationData":[OSD([sQuery(id+"F24.wireOp",EDGE,"E25.bottom"),sQuery(id+"F24.wireOp",EDGE,"E25.top"),sQuery(id+"F24.wireOp",EDGE,"E25.left"),sQuery(id+"F24.wireOp",EDGE,"E25.right")])]});
            var Q7;
            Q7=makeQuery(id+"F31.opExtrude","SWEPT_BODY",BODY,{"disambiguationData":[OSD([sQuery(id+"F30.wireOp",EDGE,"E26"),sQuery(id+"F30.wireOp",EDGE,"E27"),sQuery(id+"F30.wireOp",EDGE,"E28")])]});
            var Q8;
            Q8=makeQuery(id+"F34.opExtrude","SWEPT_BODY",BODY,{"disambiguationData":[OSD([sQuery(id+"F33.wireOp",EDGE,"E32"),sQuery(id+"F33.wireOp",EDGE,"E35"),sQuery(id+"F33.wireOp",EDGE,"E36"),sQuery(id+"F33.wireOp",EDGE,"E37"),sQuery(id+"F33.wireOp",EDGE,"E38"),sQuery(id+"F33.wireOp",EDGE,"E40"),sQuery(id+"F33.wireOp",EDGE,"E41"),sQuery(id+"F33.wireOp",EDGE,"E42"),sQuery(id+"F33.wireOp",EDGE,"E43")])]});
            var Q9;
            Q9=makeQuery(id+"F37.opPattern","COPY",BODY,{"derivedFrom":makeQuery(id+"F22.opExtrude","SWEPT_BODY",BODY,{"disambiguationData":[OSD([sQuery(id+"F21.wireOp",EDGE,"E19"),sQuery(id+"F21.wireOp",EDGE,"E21"),sQuery(id+"F21.wireOp",EDGE,"E22"),sQuery(id+"F21.wireOp",EDGE,"E20")])]}),"instanceName":"1"});
            var Q10;
            Q10=makeQuery(id+"F37.opPattern","COPY",BODY,{"derivedFrom":makeQuery(id+"F31.opExtrude","SWEPT_BODY",BODY,{"disambiguationData":[OSD([sQuery(id+"F30.wireOp",EDGE,"E26"),sQuery(id+"F30.wireOp",EDGE,"E27"),sQuery(id+"F30.wireOp",EDGE,"E28")])]}),"instanceName":"1"});
            var Q11;
            Q11=makeQuery(id+"F37.opPattern","COPY",BODY,{"derivedFrom":makeQuery(id+"F34.opExtrude","SWEPT_BODY",BODY,{"disambiguationData":[OSD([sQuery(id+"F33.wireOp",EDGE,"E32"),sQuery(id+"F33.wireOp",EDGE,"E35"),sQuery(id+"F33.wireOp",EDGE,"E36"),sQuery(id+"F33.wireOp",EDGE,"E37"),sQuery(id+"F33.wireOp",EDGE,"E38"),sQuery(id+"F33.wireOp",EDGE,"E40"),sQuery(id+"F33.wireOp",EDGE,"E41"),sQuery(id+"F33.wireOp",EDGE,"E42"),sQuery(id+"F33.wireOp",EDGE,"E43")])]}),"instanceName":"1"});
            var Q12;
            Q12=makeQuery(id+"F1.opExtrude","SWEPT_FACE",FACE,{"disambiguationData":[OSD([sQuery(id+"F0.wireOp",EDGE,"E0")])]});
            transform(context, id + "F38", {"entities" : qUnion([Q0, Q1, Q2, Q3, Q4, Q5, Q6, Q7, Q8, Q9, Q10, Q11]), "transformType" : TransformType.ROTATION, "transformAxis" : qUnion([Q12]), "angle" : 180 * degree, "makeCopy" : true});
        }
        {
            var Q0;
            Q0=qCreatedBy(makeId("Top.planeOp"),FACE);
            var sketch = newSketch(context, id + "F39", { "sketchPlane" : qUnion([Q0])});
            skCircle(sketch, "E44.0", {"center": v(0, 0) * mm, "radius": 50.8 * mm});
            skCircle(sketch, "E45.0", {"center": v(0, 0) * mm, "radius": 53.98 * mm});
            skSolve(sketch);
        }
        {
            var Q0;
            Q0=makeQuery(id+"F39.imprint","IMPRINT",FACE,{"disambiguationData":[TD([[makeQuery(id+"F39.imprint","IMPRINT",EDGE,{"derivedFrom":sQuery(id+"F39.wireOp",EDGE,"E44.0")}),-1.0]])]});
            extrude(context, id + "F40", {"entities" : qUnion([Q0]), "oppositeDirection" : true, "depth" : 6.35 * mm});
        }
        {
            var Q0;
            Q0=qCreatedBy(makeId("Right.planeOp"),FACE);
            var sketch = newSketch(context, id + "F41", { "sketchPlane" : qUnion([Q0])});
            skPoint(sketch, "E46.third.point", {"position": v(-138.86, 138.48) * mm});
            skLineSegment(sketch, "E47", {"start": v(-53.1, -6.4) * mm, "end": v(2.03, -6.3) * mm});
            skLineSegment(sketch, "E48", {"start": v(0, -6.31) * mm, "end": v(0, -17.48) * mm});
            skLineSegment(sketch, "E49.0", {"start": v(-53.98, 0) * mm, "end": v(53.98, 0) * mm});
            skLineSegment(sketch, "E50", {"start": v(0, 0) * mm, "end": v(0, -6.31) * mm});
            skFitSpline(sketch, "E51", {"points": [v(0, -17.48) * mm, v(-53.1, -6.4) * mm], "startDerivative": vector(-39.58, -0.42) * mm, "endDerivative": vector(-25.52, 23.34) * mm});
            skSolve(sketch);
        }
        {
            var Q0;
            Q0=makeQuery(id+"F41.imprint","IMPRINT",FACE,{"disambiguationData":[TD([[makeQuery(id+"F41.imprint","IMPRINT",EDGE,{"derivedFrom":sQuery(id+"F41.wireOp",EDGE,"E47")}),-1.0]])]});
            var Q1;
            Q1=sQuery(id+"F41.wireOp",EDGE,"E48");
            revolve(context, id + "F42", {"entities" : qUnion([Q0]), "axis" : qUnion([Q1]), "revolveType" : RevolveType.FULL});
        }
        {
            var Q0;
            Q0=makeQuery(id+"F1.opExtrude","SWEPT_BODY",BODY,{"disambiguationData":[OSD([sQuery(id+"F0.wireOp",EDGE,"E0"),sQuery(id+"F0.wireOp",EDGE,"E1")])]});
            var Q1;
            Q1=makeQuery(id+"F5.opExtrude","SWEPT_BODY",BODY,{"disambiguationData":[OSD([sQuery(id+"F4.wireOp",EDGE,"E2"),sQuery(id+"F4.wireOp",EDGE,"E3")])]});
            var Q2;
            Q2=makeQuery(id+"F42.opRevolve","SWEPT_BODY",BODY,{"disambiguationData":[OSD([sQuery(id+"F41.wireOp",EDGE,"E46"),sQuery(id+"F41.wireOp",EDGE,"E47"),sQuery(id+"F41.wireOp",EDGE,"E48")])]});
            var Q3;
            Q3=makeQuery(id+"F40.opExtrude","SWEPT_BODY",BODY,{"disambiguationData":[OSD([sQuery(id+"F39.wireOp",EDGE,"E44.0"),sQuery(id+"F39.wireOp",EDGE,"E45.0")])]});
            var Q4;
            Q4=makeQuery(id+"F16.opFillet","BLEND_FACE",FACE,{"disambiguationData":[OSD([sQuery(id+"F13.wireOp",EDGE,"E16")])]});
            transform(context, id + "F43", {"entities" : qUnion([Q0, Q1, Q2, Q3]), "transformType" : TransformType.ROTATION, "transformAxis" : qUnion([Q4]), "angle" : 10 * degree, "makeCopy" : false});
        }
        {
            var Q0;
            Q0=makeQuery(id+"F12.opExtrude","SWEPT_FACE",FACE,{"disambiguationData":[OSD([sQuery(id+"F11.wireOp",EDGE,"E14.top")])]});
            cPlane(context, id + "F44", {"entities" : qUnion([Q0]), "cplaneType" : CPlaneType.OFFSET, "offset" : 19.05 * mm, "oppositeDirection" : true, "width" : 152.4 * mm, "height" : 152.4 * mm});
        }
        {
            var Q0;
            Q0=qCreatedBy(id+"F44.planeOp",FACE);
            var sketch = newSketch(context, id + "F45", { "sketchPlane" : qUnion([Q0])});
            skLineSegment(sketch, "E52", {"start": v(0, 3.55) * mm, "end": v(0, 12) * mm});
            skCircle(sketch, "E53", {"center": v(0, 12) * mm, "radius": 5.72 * mm});
            skSolve(sketch);
        }
        {
            var Q0;
            Q0=qSketchRegion(id+"F45",true);
            extrude(context, id + "F46", {"entities" : qUnion([Q0]), "operationType" : NewBodyOperationType.REMOVE, "depth" : 152.4 * mm});
        }
        {
            var Q0;
            Q0=qSketchRegion(id+"F45",true);
            extrude(context, id + "F47", {"entities" : qUnion([Q0]), "operationType" : NewBodyOperationType.ADD, "depth" : 152.4 * mm, "offsetDistance" : 25.4 * mm});
        }
        {
            var Q0;
            Q0=makeQuery(id+"F1.opExtrude","CAP_FACE",FACE,{"disambiguationData":[OSD([sQuery(id+"F0.wireOp",EDGE,"E0"),sQuery(id+"F0.wireOp",EDGE,"E1")])],"isStart":false});
            cPlane(context, id + "F48", {"entities" : qUnion([Q0]), "cplaneType" : CPlaneType.OFFSET, "offset" : 0 * mm, "width" : 152.4 * mm, "height" : 152.4 * mm});
        }
        {
            var Q0;
            Q0=makeQuery(id+"F47.opExtrude","SWEPT_BODY",BODY,{"disambiguationData":[OSD([sQuery(id+"F45.wireOp",EDGE,"E53")])]});
            var Q1;
            Q1=makeQuery(id+"FaXGfu7BxXb7jBO_24.opRevolve","SWEPT_BODY",BODY,{"disambiguationData":[OSD([sQuery(id+"FF98HWkuvTNxnMc_24.wireOp",EDGE,"49LvXQ14-6qvC-DYei-XO3c-WQOcWccngW4j"),sQuery(id+"FF98HWkuvTNxnMc_24.wireOp",EDGE,"eAGRftWs-R22p-PTR0-D9Ip-pdIuIoDzmrJa"),sQuery(id+"FF98HWkuvTNxnMc_24.wireOp",EDGE,"8a8N54Aw-W0BB-wZ1P-kggP-A0rt618bdvBl")])]});
            var Q2;
            Q2=makeQuery(id+"F40.opExtrude","SWEPT_BODY",BODY,{"disambiguationData":[OSD([sQuery(id+"F39.wireOp",EDGE,"E44.0"),sQuery(id+"F39.wireOp",EDGE,"E45.0")])]});
            var Q3;
            Q3=makeQuery(id+"F38.opPattern","COPY",BODY,{"derivedFrom":makeQuery(id+"F37.opPattern","COPY",BODY,{"derivedFrom":makeQuery(id+"F34.opExtrude","SWEPT_BODY",BODY,{"disambiguationData":[OSD([sQuery(id+"F33.wireOp",EDGE,"E32"),sQuery(id+"F33.wireOp",EDGE,"E35"),sQuery(id+"F33.wireOp",EDGE,"E36"),sQuery(id+"F33.wireOp",EDGE,"E37"),sQuery(id+"F33.wireOp",EDGE,"E38"),sQuery(id+"F33.wireOp",EDGE,"E40"),sQuery(id+"F33.wireOp",EDGE,"E41"),sQuery(id+"F33.wireOp",EDGE,"E42"),sQuery(id+"F33.wireOp",EDGE,"E43")])]}),"instanceName":"1"}),"instanceName":"1"});
            var Q4;
            Q4=makeQuery(id+"F38.opPattern","COPY",BODY,{"derivedFrom":makeQuery(id+"F37.opPattern","COPY",BODY,{"derivedFrom":makeQuery(id+"F31.opExtrude","SWEPT_BODY",BODY,{"disambiguationData":[OSD([sQuery(id+"F30.wireOp",EDGE,"E27"),sQuery(id+"F30.wireOp",EDGE,"E28")])]}),"instanceName":"1"}),"instanceName":"1"});
            var Q5;
            Q5=makeQuery(id+"F38.opPattern","COPY",BODY,{"derivedFrom":makeQuery(id+"F37.opPattern","COPY",BODY,{"derivedFrom":makeQuery(id+"F22.opExtrude","SWEPT_BODY",BODY,{"disambiguationData":[OSD([sQuery(id+"F21.wireOp",EDGE,"E19"),sQuery(id+"F21.wireOp",EDGE,"E21"),sQuery(id+"F21.wireOp",EDGE,"E22"),sQuery(id+"F21.wireOp",EDGE,"E20")])]}),"instanceName":"1"}),"instanceName":"1"});
            var Q6;
            Q6=makeQuery(id+"F38.opPattern","COPY",BODY,{"derivedFrom":makeQuery(id+"F34.opExtrude","SWEPT_BODY",BODY,{"disambiguationData":[OSD([sQuery(id+"F33.wireOp",EDGE,"E32"),sQuery(id+"F33.wireOp",EDGE,"E35"),sQuery(id+"F33.wireOp",EDGE,"E36"),sQuery(id+"F33.wireOp",EDGE,"E37"),sQuery(id+"F33.wireOp",EDGE,"E38"),sQuery(id+"F33.wireOp",EDGE,"E40"),sQuery(id+"F33.wireOp",EDGE,"E41"),sQuery(id+"F33.wireOp",EDGE,"E42"),sQuery(id+"F33.wireOp",EDGE,"E43")])]}),"instanceName":"1"});
            var Q7;
            Q7=makeQuery(id+"F38.opPattern","COPY",BODY,{"derivedFrom":makeQuery(id+"F31.opExtrude","SWEPT_BODY",BODY,{"disambiguationData":[OSD([sQuery(id+"F30.wireOp",EDGE,"E27"),sQuery(id+"F30.wireOp",EDGE,"E28")])]}),"instanceName":"1"});
            var Q8;
            Q8=makeQuery(id+"F38.opPattern","COPY",BODY,{"derivedFrom":makeQuery(id+"F25.opExtrude","SWEPT_BODY",BODY,{"disambiguationData":[OSD([sQuery(id+"F24.wireOp",EDGE,"E25.bottom"),sQuery(id+"F24.wireOp",EDGE,"E25.top"),sQuery(id+"F24.wireOp",EDGE,"E25.left"),sQuery(id+"F24.wireOp",EDGE,"E25.right")])]}),"instanceName":"1"});
            var Q9;
            Q9=makeQuery(id+"F38.opPattern","COPY",BODY,{"derivedFrom":makeQuery(id+"F22.opExtrude","SWEPT_BODY",BODY,{"disambiguationData":[OSD([sQuery(id+"F21.wireOp",EDGE,"E19"),sQuery(id+"F21.wireOp",EDGE,"E21"),sQuery(id+"F21.wireOp",EDGE,"E22"),sQuery(id+"F21.wireOp",EDGE,"E20")])]}),"instanceName":"1"});
            var Q10;
            Q10=makeQuery(id+"F38.opPattern","COPY",BODY,{"derivedFrom":makeQuery(id+"F15.opExtrude","SWEPT_BODY",BODY,{"disambiguationData":[OSD([sQuery(id+"F13.wireOp",EDGE,"E15"),sQuery(id+"F13.wireOp",EDGE,"E16")])]}),"instanceName":"1"});
            var Q11;
            Q11=makeQuery(id+"F38.opPattern","COPY",BODY,{"derivedFrom":makeQuery(id+"F14.opExtrude","SWEPT_BODY",BODY,{"disambiguationData":[OSD([sQuery(id+"F13.wireOp",EDGE,"E16")])]}),"instanceName":"1"});
            var Q12;
            Q12=makeQuery(id+"F38.opPattern","COPY",BODY,{"derivedFrom":makeQuery(id+"F12.opExtrude","SWEPT_BODY",BODY,{"disambiguationData":[OSD([sQuery(id+"F11.wireOp",EDGE,"E14.bottom"),sQuery(id+"F11.wireOp",EDGE,"E14.top"),sQuery(id+"F11.wireOp",EDGE,"E14.left"),sQuery(id+"F11.wireOp",EDGE,"E14.right")])]}),"instanceName":"1"});
            var Q13;
            Q13=makeQuery(id+"F38.opPattern","COPY",BODY,{"derivedFrom":makeQuery(id+"F8.opExtrude","SWEPT_BODY",BODY,{"disambiguationData":[OSD([sQuery(id+"F7.wireOp",EDGE,"E4"),sQuery(id+"F7.wireOp",EDGE,"E5")])]}),"instanceName":"1"});
            var Q14;
            Q14=makeQuery(id+"F37.opPattern","COPY",BODY,{"derivedFrom":makeQuery(id+"F34.opExtrude","SWEPT_BODY",BODY,{"disambiguationData":[OSD([sQuery(id+"F33.wireOp",EDGE,"E32"),sQuery(id+"F33.wireOp",EDGE,"E35"),sQuery(id+"F33.wireOp",EDGE,"E36"),sQuery(id+"F33.wireOp",EDGE,"E37"),sQuery(id+"F33.wireOp",EDGE,"E38"),sQuery(id+"F33.wireOp",EDGE,"E40"),sQuery(id+"F33.wireOp",EDGE,"E41"),sQuery(id+"F33.wireOp",EDGE,"E42"),sQuery(id+"F33.wireOp",EDGE,"E43")])]}),"instanceName":"1"});
            var Q15;
            Q15=makeQuery(id+"F37.opPattern","COPY",BODY,{"derivedFrom":makeQuery(id+"F31.opExtrude","SWEPT_BODY",BODY,{"disambiguationData":[OSD([sQuery(id+"F30.wireOp",EDGE,"E27"),sQuery(id+"F30.wireOp",EDGE,"E28")])]}),"instanceName":"1"});
            var Q16;
            Q16=makeQuery(id+"F37.opPattern","COPY",BODY,{"derivedFrom":makeQuery(id+"F22.opExtrude","SWEPT_BODY",BODY,{"disambiguationData":[OSD([sQuery(id+"F21.wireOp",EDGE,"E19"),sQuery(id+"F21.wireOp",EDGE,"E21"),sQuery(id+"F21.wireOp",EDGE,"E22"),sQuery(id+"F21.wireOp",EDGE,"E20")])]}),"instanceName":"1"});
            var Q17;
            Q17=makeQuery(id+"F34.opExtrude","SWEPT_BODY",BODY,{"disambiguationData":[OSD([sQuery(id+"F33.wireOp",EDGE,"E32"),sQuery(id+"F33.wireOp",EDGE,"E35"),sQuery(id+"F33.wireOp",EDGE,"E36"),sQuery(id+"F33.wireOp",EDGE,"E37"),sQuery(id+"F33.wireOp",EDGE,"E38"),sQuery(id+"F33.wireOp",EDGE,"E40"),sQuery(id+"F33.wireOp",EDGE,"E41"),sQuery(id+"F33.wireOp",EDGE,"E42"),sQuery(id+"F33.wireOp",EDGE,"E43")])]});
            var Q18;
            Q18=makeQuery(id+"F25.opExtrude","SWEPT_BODY",BODY,{"disambiguationData":[OSD([sQuery(id+"F24.wireOp",EDGE,"E25.bottom"),sQuery(id+"F24.wireOp",EDGE,"E25.top"),sQuery(id+"F24.wireOp",EDGE,"E25.left"),sQuery(id+"F24.wireOp",EDGE,"E25.right")])]});
            var Q19;
            Q19=makeQuery(id+"F22.opExtrude","SWEPT_BODY",BODY,{"disambiguationData":[OSD([sQuery(id+"F21.wireOp",EDGE,"E19"),sQuery(id+"F21.wireOp",EDGE,"E21"),sQuery(id+"F21.wireOp",EDGE,"E22"),sQuery(id+"F21.wireOp",EDGE,"E20")])]});
            var Q20;
            Q20=makeQuery(id+"F1.opExtrude","SWEPT_BODY",BODY,{"disambiguationData":[OSD([sQuery(id+"F0.wireOp",EDGE,"E0"),sQuery(id+"F0.wireOp",EDGE,"E1")])]});
            var Q21;
            Q21=makeQuery(id+"F5.opExtrude","SWEPT_BODY",BODY,{"disambiguationData":[OSD([sQuery(id+"F4.wireOp",EDGE,"E2"),sQuery(id+"F4.wireOp",EDGE,"E3")])]});
            var Q22;
            Q22=makeQuery(id+"F8.opExtrude","SWEPT_BODY",BODY,{"disambiguationData":[OSD([sQuery(id+"F7.wireOp",EDGE,"E4"),sQuery(id+"F7.wireOp",EDGE,"E5")])]});
            var Q23;
            Q23=makeQuery(id+"F12.opExtrude","SWEPT_BODY",BODY,{"disambiguationData":[OSD([sQuery(id+"F11.wireOp",EDGE,"E14.bottom"),sQuery(id+"F11.wireOp",EDGE,"E14.top"),sQuery(id+"F11.wireOp",EDGE,"E14.left"),sQuery(id+"F11.wireOp",EDGE,"E14.right")])]});
            var Q24;
            Q24=makeQuery(id+"Ff6Yrm0YfJ8zp5a_26.opExtrude","SWEPT_BODY",BODY,{"disambiguationData":[OSD([sQuery(id+"F1kwTX1hUvt4jwI_26.wireOp",EDGE,"ddeee0c3-f45c-4f39-a296-87449217fdd8.0")])]});
            var Q25;
            Q25=makeQuery(id+"F42.opRevolve","SWEPT_BODY",BODY,{"disambiguationData":[OSD([sQuery(id+"F41.wireOp",EDGE,"E47"),sQuery(id+"F41.wireOp",EDGE,"E48"),sQuery(id+"F41.wireOp",EDGE,"UB6mWWp6-jujb-jPiI-BXFH-pHugUafLUuwH")])]});
            var Q26;
            Q26=makeQuery(id+"F31.opExtrude","SWEPT_BODY",BODY,{"disambiguationData":[OSD([sQuery(id+"F30.wireOp",EDGE,"E27"),sQuery(id+"F30.wireOp",EDGE,"E28")])]});
            var Q27;
            Q27=makeQuery(id+"F14.opExtrude","SWEPT_BODY",BODY,{"disambiguationData":[OSD([sQuery(id+"F13.wireOp",EDGE,"E16")])]});
            var Q28;
            Q28=makeQuery(id+"F15.opExtrude","SWEPT_BODY",BODY,{"disambiguationData":[OSD([sQuery(id+"F13.wireOp",EDGE,"E15"),sQuery(id+"F13.wireOp",EDGE,"E16")])]});
            var Q29;
            Q29=makeQuery(id+"Ff6Yrm0YfJ8zp5a_26.opExtrude","SWEPT_BODY",BODY,{"disambiguationData":[OSD([sQuery(id+"F1kwTX1hUvt4jwI_26.wireOp",EDGE,"d68bfbfc-8b63-4e16-ae6c-958f549a9e9b.0")])]});
            var Q30;
            {var subQ0=sQuery(id+"F11.wireOp",EDGE,"E14.right");var subQ1=sQuery(id+"F11.wireOp",EDGE,"E14.top");Q30=makeQuery(id+"F27.opChamfer","BLEND_VERTEX",VERTEX,{"blendedFrom":[makeQuery(id+"F12.opExtrude","SWEPT_EDGE",EDGE,{"disambiguationData":[OSD([subQ1,subQ0])]}),makeQuery(id+"F12.opExtrude","CAP_FACE",FACE,{"disambiguationData":[OSD([sQuery(id+"F11.wireOp",EDGE,"E14.bottom"),subQ1,sQuery(id+"F11.wireOp",EDGE,"E14.left"),subQ0])],"isStart":false}),makeQuery(id+"F12.opExtrude","SWEPT_FACE",FACE,{"disambiguationData":[OSD([subQ0])]})],"blendedInto":[makeQuery(id+"F12.opExtrude","CAP_FACE",FACE,{"disambiguationData":[OSD([sQuery(id+"F11.wireOp",EDGE,"E14.bottom"),subQ1,sQuery(id+"F11.wireOp",EDGE,"E14.left"),subQ0])],"isStart":false}),makeQuery(id+"F12.opExtrude","SWEPT_FACE",FACE,{"disambiguationData":[OSD([subQ0])]})]});}
            transform(context, id + "F49", {"entities" : qUnion([Q0, Q1, Q2, Q3, Q4, Q5, Q6, Q7, Q8, Q9, Q10, Q11, Q12, Q13, Q14, Q15, Q16, Q17, Q18, Q19, Q20, Q21, Q22, Q23, Q24, Q25, Q26, Q27, Q28, Q29]), "transformType" : TransformType.SCALE_UNIFORMLY, "scale" : .444444, "scalePoint" : qUnion([Q30]), "makeCopy" : false});
        }
        {
            var Q0;
            Q0=makeQuery(id+"F1.opExtrude","SWEPT_BODY",BODY,{"disambiguationData":[OSD([sQuery(id+"F0.wireOp",EDGE,"E0"),sQuery(id+"F0.wireOp",EDGE,"E1")])]});
            var Q1;
            Q1=makeQuery(id+"F38.opPattern","COPY",BODY,{"derivedFrom":makeQuery(id+"F12.opExtrude","SWEPT_BODY",BODY,{"disambiguationData":[OSD([sQuery(id+"F11.wireOp",EDGE,"E14.bottom"),sQuery(id+"F11.wireOp",EDGE,"E14.top"),sQuery(id+"F11.wireOp",EDGE,"E14.left"),sQuery(id+"F11.wireOp",EDGE,"E14.right")])]}),"instanceName":"1"});
            var Q2;
            Q2=makeQuery(id+"F42.opRevolve","SWEPT_BODY",BODY,{"disambiguationData":[OSD([sQuery(id+"F41.wireOp",EDGE,"E47"),sQuery(id+"F41.wireOp",EDGE,"E48"),sQuery(id+"F41.wireOp",EDGE,"E51")])]});
            var Q3;
            Q3=makeQuery(id+"F38.opPattern","COPY",BODY,{"derivedFrom":makeQuery(id+"F37.opPattern","COPY",BODY,{"derivedFrom":makeQuery(id+"F22.opExtrude","SWEPT_BODY",BODY,{"disambiguationData":[OSD([sQuery(id+"F21.wireOp",EDGE,"E19"),sQuery(id+"F21.wireOp",EDGE,"E21"),sQuery(id+"F21.wireOp",EDGE,"E22"),sQuery(id+"F21.wireOp",EDGE,"E20")])]}),"instanceName":"1"}),"instanceName":"1"});
            var Q4;
            Q4=makeQuery(id+"F38.opPattern","COPY",BODY,{"derivedFrom":makeQuery(id+"F37.opPattern","COPY",BODY,{"derivedFrom":makeQuery(id+"F34.opExtrude","SWEPT_BODY",BODY,{"disambiguationData":[OSD([sQuery(id+"F33.wireOp",EDGE,"E32"),sQuery(id+"F33.wireOp",EDGE,"E35"),sQuery(id+"F33.wireOp",EDGE,"E36"),sQuery(id+"F33.wireOp",EDGE,"E37"),sQuery(id+"F33.wireOp",EDGE,"E38"),sQuery(id+"F33.wireOp",EDGE,"E40"),sQuery(id+"F33.wireOp",EDGE,"E41"),sQuery(id+"F33.wireOp",EDGE,"E42"),sQuery(id+"F33.wireOp",EDGE,"E43")])]}),"instanceName":"1"}),"instanceName":"1"});
            var Q5;
            Q5=makeQuery(id+"F12.opExtrude","SWEPT_BODY",BODY,{"disambiguationData":[OSD([sQuery(id+"F11.wireOp",EDGE,"E14.bottom"),sQuery(id+"F11.wireOp",EDGE,"E14.top"),sQuery(id+"F11.wireOp",EDGE,"E14.left"),sQuery(id+"F11.wireOp",EDGE,"E14.right")])]});
            var Q6;
            Q6=makeQuery(id+"F8.opExtrude","SWEPT_BODY",BODY,{"disambiguationData":[OSD([sQuery(id+"F7.wireOp",EDGE,"E4"),sQuery(id+"F7.wireOp",EDGE,"E5")])]});
            var Q7;
            Q7=makeQuery(id+"F34.opExtrude","SWEPT_BODY",BODY,{"disambiguationData":[OSD([sQuery(id+"F33.wireOp",EDGE,"E32"),sQuery(id+"F33.wireOp",EDGE,"E35"),sQuery(id+"F33.wireOp",EDGE,"E36"),sQuery(id+"F33.wireOp",EDGE,"E37"),sQuery(id+"F33.wireOp",EDGE,"E38"),sQuery(id+"F33.wireOp",EDGE,"E40"),sQuery(id+"F33.wireOp",EDGE,"E41"),sQuery(id+"F33.wireOp",EDGE,"E42"),sQuery(id+"F33.wireOp",EDGE,"E43")])]});
            var Q8;
            Q8=makeQuery(id+"F40.opExtrude","SWEPT_BODY",BODY,{"disambiguationData":[OSD([sQuery(id+"F39.wireOp",EDGE,"E44.0"),sQuery(id+"F39.wireOp",EDGE,"E45.0")])]});
            var Q9;
            Q9=makeQuery(id+"F22.opExtrude","SWEPT_BODY",BODY,{"disambiguationData":[OSD([sQuery(id+"F21.wireOp",EDGE,"E19"),sQuery(id+"F21.wireOp",EDGE,"E21"),sQuery(id+"F21.wireOp",EDGE,"E22"),sQuery(id+"F21.wireOp",EDGE,"E20")])]});
            var Q10;
            Q10=makeQuery(id+"F37.opPattern","COPY",BODY,{"derivedFrom":makeQuery(id+"F22.opExtrude","SWEPT_BODY",BODY,{"disambiguationData":[OSD([sQuery(id+"F21.wireOp",EDGE,"E19"),sQuery(id+"F21.wireOp",EDGE,"E21"),sQuery(id+"F21.wireOp",EDGE,"E22"),sQuery(id+"F21.wireOp",EDGE,"E20")])]}),"instanceName":"1"});
            var Q11;
            Q11=makeQuery(id+"F37.opPattern","COPY",BODY,{"derivedFrom":makeQuery(id+"F34.opExtrude","SWEPT_BODY",BODY,{"disambiguationData":[OSD([sQuery(id+"F33.wireOp",EDGE,"E32"),sQuery(id+"F33.wireOp",EDGE,"E35"),sQuery(id+"F33.wireOp",EDGE,"E36"),sQuery(id+"F33.wireOp",EDGE,"E37"),sQuery(id+"F33.wireOp",EDGE,"E38"),sQuery(id+"F33.wireOp",EDGE,"E40"),sQuery(id+"F33.wireOp",EDGE,"E41"),sQuery(id+"F33.wireOp",EDGE,"E42"),sQuery(id+"F33.wireOp",EDGE,"E43")])]}),"instanceName":"1"});
            var Q12;
            Q12=makeQuery(id+"F38.opPattern","COPY",BODY,{"derivedFrom":makeQuery(id+"F8.opExtrude","SWEPT_BODY",BODY,{"disambiguationData":[OSD([sQuery(id+"F7.wireOp",EDGE,"E4"),sQuery(id+"F7.wireOp",EDGE,"E5")])]}),"instanceName":"1"});
            var Q13;
            Q13=makeQuery(id+"F38.opPattern","COPY",BODY,{"derivedFrom":makeQuery(id+"F34.opExtrude","SWEPT_BODY",BODY,{"disambiguationData":[OSD([sQuery(id+"F33.wireOp",EDGE,"E32"),sQuery(id+"F33.wireOp",EDGE,"E35"),sQuery(id+"F33.wireOp",EDGE,"E36"),sQuery(id+"F33.wireOp",EDGE,"E37"),sQuery(id+"F33.wireOp",EDGE,"E38"),sQuery(id+"F33.wireOp",EDGE,"E40"),sQuery(id+"F33.wireOp",EDGE,"E41"),sQuery(id+"F33.wireOp",EDGE,"E42"),sQuery(id+"F33.wireOp",EDGE,"E43")])]}),"instanceName":"1"});
            var Q14;
            Q14=makeQuery(id+"F38.opPattern","COPY",BODY,{"derivedFrom":makeQuery(id+"F22.opExtrude","SWEPT_BODY",BODY,{"disambiguationData":[OSD([sQuery(id+"F21.wireOp",EDGE,"E19"),sQuery(id+"F21.wireOp",EDGE,"E21"),sQuery(id+"F21.wireOp",EDGE,"E22"),sQuery(id+"F21.wireOp",EDGE,"E20")])]}),"instanceName":"1"});
            var Q15;
            Q15=sQuery(id+"F41.wireOp",VERTEX,"E49.0.end");
            transform(context, id + "F50", {"entities" : qUnion([Q0, Q1, Q2, Q3, Q4, Q5, Q6, Q7, Q8, Q9, Q10, Q11, Q12, Q13, Q14]), "transformType" : TransformType.SCALE_UNIFORMLY, "scale" : 10, "scalePoint" : qUnion([Q15]), "makeCopy" : false});
        }
    });
